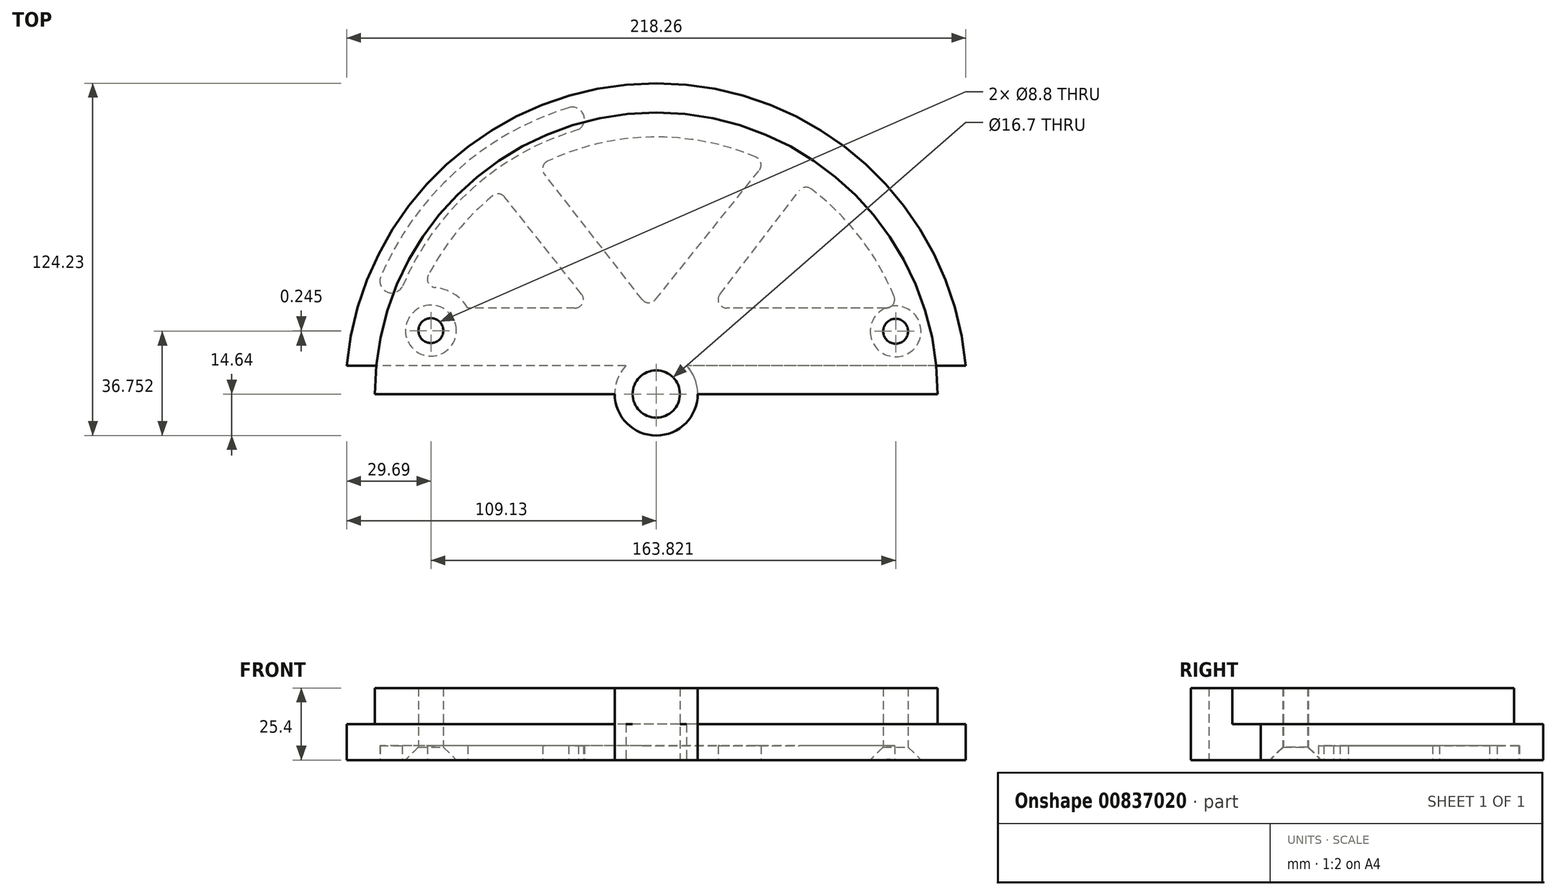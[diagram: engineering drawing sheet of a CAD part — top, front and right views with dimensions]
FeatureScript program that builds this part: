
annotation { "Feature Type Name" : "Feature", "Feature Type Description" : "" }
export const myFeature = defineFeature(function(context is Context, id is Id, definition is map)
    precondition{}
    {
        {
            var Q0;
            Q0=qCreatedBy(makeId("Top.planeOp"),FACE);
            var sketch = newSketch(context, id + "F0", { "sketchPlane" : qUnion([Q0])});
            skArc(sketch, "E0", {"start": v(109.6, 0) * mm, "mid": v(0, 109.6) * mm, "end": v(-109.6, 0) * mm});
            skLineSegment(sketch, "E1", {"start": v(-109.6, 0) * mm, "end": v(109.6, 0) * mm});
            skSolve(sketch);
        }
        {
            var Q0;
            Q0=makeQuery(id+"F0.imprint","IMPRINT",FACE,{"disambiguationData":[TD([[makeQuery(id+"F0.imprint","IMPRINT",EDGE,{"derivedFrom":sQuery(id+"F0.wireOp",EDGE,"E0")}),1.0]])]});
            extrude(context, id + "F1", {"entities" : qUnion([Q0]), "depth" : 12.7 * mm, "offsetDistance" : 25.4 * mm});
        }
        {
            var Q0;
            Q0=qCreatedBy(makeId("Top.planeOp"),FACE);
            var sketch = newSketch(context, id + "F2", { "sketchPlane" : qUnion([Q0])});
            skArc(sketch, "E2", {"start": v(99.24, 0) * mm, "mid": v(0, 99.24) * mm, "end": v(-99.24, 0) * mm});
            skLineSegment(sketch, "E3", {"start": v(99.24, 0) * mm, "end": v(-99.24, 0) * mm});
            skSolve(sketch);
        }
        {
            var Q0;
            Q0=makeQuery(id+"F2.imprint","IMPRINT",FACE,{"disambiguationData":[TD([[makeQuery(id+"F2.imprint","IMPRINT",EDGE,{"derivedFrom":sQuery(id+"F2.wireOp",EDGE,"E2")}),1.0]])]});
            extrude(context, id + "F3", {"entities" : qUnion([Q0]), "operationType" : NewBodyOperationType.ADD, "depth" : 25.4 * mm, "offsetDistance" : 25.4 * mm});
        }
        {
            var Q0;
            Q0=qCreatedBy(makeId("Top.planeOp"),FACE);
            var sketch = newSketch(context, id + "F4", { "sketchPlane" : qUnion([Q0])});
            skLineSegment(sketch, "E4.bottom", {"start": v(116.9, 10.04) * mm, "end": v(-125.87, 10.04) * mm});
            skLineSegment(sketch, "E4.top", {"start": v(116.9, -20) * mm, "end": v(-125.87, -20) * mm});
            skLineSegment(sketch, "E4.left", {"start": v(116.9, 10.04) * mm, "end": v(116.9, -20) * mm});
            skLineSegment(sketch, "E4.right", {"start": v(-125.87, 10.04) * mm, "end": v(-125.87, -20) * mm});
            skSolve(sketch);
        }
        {
            var Q0;
            Q0=makeQuery(id+"F4.imprint","IMPRINT",FACE,{"disambiguationData":[TD([[makeQuery(id+"F4.imprint","IMPRINT",EDGE,{"derivedFrom":sQuery(id+"F4.wireOp",EDGE,"E4.bottom")}),1.0]])]});
            extrude(context, id + "F5", {"entities" : qUnion([Q0]), "operationType" : NewBodyOperationType.REMOVE, "depth" : 12.7 * mm, "offsetDistance" : 25.4 * mm});
        }
        {
            var Q0;
            Q0=qCreatedBy(makeId("Top.planeOp"),FACE);
            var sketch = newSketch(context, id + "F6", { "sketchPlane" : qUnion([Q0])});
            skCircle(sketch, "E5", {"center": v(0, 0) * mm, "radius": 14.64 * mm});
            skSolve(sketch);
        }
        {
            var Q0;
            Q0=makeQuery(id+"F6.imprint","IMPRINT",FACE,{"disambiguationData":[TD([[makeQuery(id+"F6.imprint","IMPRINT",EDGE,{"derivedFrom":sQuery(id+"F6.wireOp",EDGE,"E5")}),1.0]])]});
            extrude(context, id + "F7", {"entities" : qUnion([Q0]), "operationType" : NewBodyOperationType.ADD, "depth" : 25.4 * mm, "offsetDistance" : 25.4 * mm});
        }
        {
            var Q0;
            Q0=qCreatedBy(makeId("Top.planeOp"),FACE);
            var sketch = newSketch(context, id + "F8", { "sketchPlane" : qUnion([Q0])});
            skCircle(sketch, "E6", {"center": v(0, 0) * mm, "radius": 8.35 * mm});
            skSolve(sketch);
        }
        {
            var Q0;
            Q0=makeQuery(id+"F8.imprint","IMPRINT",FACE,{"disambiguationData":[TD([[makeQuery(id+"F8.imprint","IMPRINT",EDGE,{"derivedFrom":sQuery(id+"F8.wireOp",EDGE,"E6")}),1.0]])]});
            extrude(context, id + "F9", {"entities" : qUnion([Q0]), "operationType" : NewBodyOperationType.REMOVE, "depth" : 25.4 * mm, "offsetDistance" : 25.4 * mm});
        }
        {
            var Q0;
            Q0=qCreatedBy(makeId("Top.planeOp"),FACE);
            var sketch = newSketch(context, id + "F10", { "sketchPlane" : qUnion([Q0])});
            skArc(sketch, "E7", {"start": v(83.82, 34.46) * mm, "mid": v(71.76, 55.35) * mm, "end": v(54.62, 72.32) * mm});
            skLineSegment(sketch, "E8", {"start": v(81.04, 30.32) * mm, "end": v(24.8, 30.32) * mm});
            skLineSegment(sketch, "E9", {"start": v(22.42, 35.15) * mm, "end": v(50.43, 71.75) * mm});
            skLineSegment(sketch, "E10", {"start": v(-0.26, 33.28) * mm, "end": v(36.3, 78.9) * mm});
            skLineSegment(sketch, "E11", {"start": v(-4.97, 33.32) * mm, "end": v(-39.44, 77.55) * mm});
            skLineSegment(sketch, "E12", {"start": v(-26.3, 35.18) * mm, "end": v(-53.43, 69.44) * mm});
            skArc(sketch, "E13", {"start": v(-66.42, 30.32) * mm, "mid": v(-71.35, 35.3) * mm, "end": v(-77.97, 37.55) * mm});
            skLineSegment(sketch, "E14.trimOffspring", {"start": v(-28.65, 30.32) * mm, "end": v(-66.42, 30.32) * mm});
            skArc(sketch, "E15.trimOffspring", {"start": v(35.13, 83.54) * mm, "mid": v(-1.76, 90.6) * mm, "end": v(-38.34, 82.11) * mm});
            skArc(sketch, "E16.trimOffspring", {"start": v(-57.69, 69.9) * mm, "mid": v(-70.42, 57.04) * mm, "end": v(-80.35, 41.92) * mm});
            skPoint(sketch, "E17.visualSharp", {"position": v(-2.63, 30.32) * mm});
            skArc(sketch, "E17.filletArc", {"start": v(-4.97, 33.32) * mm, "mid": v(-2.62, 32.16) * mm, "end": v(-0.26, 33.28) * mm});
            skPoint(sketch, "E18.visualSharp", {"position": v(-22.45, 30.32) * mm});
            skArc(sketch, "E18.filletArc", {"start": v(-28.65, 30.32) * mm, "mid": v(-25.95, 32.02) * mm, "end": v(-26.3, 35.18) * mm});
            skPoint(sketch, "E19.visualSharp", {"position": v(18.73, 30.32) * mm});
            skArc(sketch, "E19.filletArc", {"start": v(22.42, 35.15) * mm, "mid": v(22.12, 32) * mm, "end": v(24.8, 30.32) * mm});
            skPoint(sketch, "E20.visualSharp", {"position": v(85.4, 30.32) * mm});
            skArc(sketch, "E20.filletArc", {"start": v(81.04, 30.32) * mm, "mid": v(83.53, 31.65) * mm, "end": v(83.82, 34.46) * mm});
            skPoint(sketch, "E21.visualSharp", {"position": v(52.2, 74.08) * mm});
            skArc(sketch, "E21.filletArc", {"start": v(54.62, 72.32) * mm, "mid": v(52.4, 72.9) * mm, "end": v(50.43, 71.75) * mm});
            skPoint(sketch, "E22.visualSharp", {"position": v(38.74, 81.93) * mm});
            skArc(sketch, "E22.filletArc", {"start": v(36.3, 78.9) * mm, "mid": v(36.88, 81.51) * mm, "end": v(35.13, 83.54) * mm});
            skPoint(sketch, "E23.visualSharp", {"position": v(-41.7, 80.46) * mm});
            skArc(sketch, "E23.filletArc", {"start": v(-38.34, 82.11) * mm, "mid": v(-39.99, 80.1) * mm, "end": v(-39.44, 77.55) * mm});
            skPoint(sketch, "E24.visualSharp", {"position": v(-55.3, 71.8) * mm});
            skArc(sketch, "E24.filletArc", {"start": v(-53.43, 69.44) * mm, "mid": v(-55.46, 70.56) * mm, "end": v(-57.69, 69.9) * mm});
            skPoint(sketch, "E25.visualSharp", {"position": v(-82.6, 37.29) * mm});
            skArc(sketch, "E25.filletArc", {"start": v(-80.35, 41.92) * mm, "mid": v(-80.32, 39.1) * mm, "end": v(-77.97, 37.55) * mm});
            skSolve(sketch);
        }
        {
            var Q0;
            Q0=makeQuery(id+"F10.imprint","IMPRINT",FACE,{"disambiguationData":[TD([[makeQuery(id+"F10.imprint","IMPRINT",EDGE,{"derivedFrom":sQuery(id+"F10.wireOp",EDGE,"E7")}),1.0]])]});
            var Q1;
            Q1=makeQuery(id+"F10.imprint","IMPRINT",FACE,{"disambiguationData":[TD([[makeQuery(id+"F10.imprint","IMPRINT",EDGE,{"derivedFrom":sQuery(id+"F10.wireOp",EDGE,"E10")}),1.0]])]});
            var Q2;
            Q2=makeQuery(id+"F10.imprint","IMPRINT",FACE,{"disambiguationData":[TD([[makeQuery(id+"F10.imprint","IMPRINT",EDGE,{"derivedFrom":sQuery(id+"F10.wireOp",EDGE,"E12")}),1.0]])]});
            extrude(context, id + "F11", {"entities" : qUnion([Q0, Q1, Q2]), "operationType" : NewBodyOperationType.REMOVE, "depth" : 5.08 * mm, "offsetDistance" : 25.4 * mm});
        }
        {
            var Q0;
            Q0=qCreatedBy(makeId("Top.planeOp"),FACE);
            var sketch = newSketch(context, id + "F12", { "sketchPlane" : qUnion([Q0])});
            skArc(sketch, "E26", {"start": v(-27.4, 93.25) * mm, "mid": v(-64.68, 72.55) * mm, "end": v(-89.5, 37.89) * mm});
            skArc(sketch, "E27", {"start": v(-30.91, 100.93) * mm, "mid": v(-70.82, 78.27) * mm, "end": v(-97.34, 40.82) * mm});
            skArc(sketch, "E28", {"start": v(-27.4, 93.25) * mm, "mid": v(-25.72, 98.66) * mm, "end": v(-30.91, 100.93) * mm});
            skArc(sketch, "E29", {"start": v(-97.34, 40.82) * mm, "mid": v(-94.7, 35.94) * mm, "end": v(-89.5, 37.89) * mm});
            skSolve(sketch);
        }
        {
            var Q0;
            Q0=makeQuery(id+"F12.imprint","IMPRINT",FACE,{"disambiguationData":[TD([[makeQuery(id+"F12.imprint","IMPRINT",EDGE,{"derivedFrom":sQuery(id+"F12.wireOp",EDGE,"E26")}),-1.0]])]});
            extrude(context, id + "F13", {"entities" : qUnion([Q0]), "operationType" : NewBodyOperationType.REMOVE, "depth" : 5.08 * mm, "offsetDistance" : 25.4 * mm});
        }
        {
            var Q0;
            Q0=makeQuery(id+"F7.boolean.opBoolean","MERGE",FACE,{"derivedFrom":[makeQuery(id+"F1.opExtrude","CAP_FACE",FACE,{"disambiguationData":[OSD([sQuery(id+"F0.wireOp",EDGE,"E0"),sQuery(id+"F0.wireOp",EDGE,"E1")])],"isStart":true}),makeQuery(id+"F7.opExtrude","CAP_FACE",FACE,{"disambiguationData":[OSD([sQuery(id+"F6.wireOp",EDGE,"E5")])],"isStart":true})]});
            var sketch = newSketch(context, id + "F14", { "sketchPlane" : qUnion([Q0])});
            skPoint(sketch, "E30", {"position": v(84.38, -22.11) * mm});
            skPoint(sketch, "E31", {"position": v(-79.44, -22.36) * mm});
            skSolve(sketch);
        }
        {
            var Q0;
            Q0=sQuery(id+"F14.wireOp",VERTEX,"E30");
            var Q1;
            Q1=sQuery(id+"F14.wireOp",VERTEX,"E31");
            var Q2;
            Q2=makeQuery(id+"F1.opExtrude","SWEPT_BODY",BODY,{"disambiguationData":[OSD([sQuery(id+"F0.wireOp",EDGE,"E0"),sQuery(id+"F0.wireOp",EDGE,"E1")])]});
            hole(context, id + "F15", {"style" : HoleStyle.C_SINK, "endStyle" : HoleEndStyle.THROUGH, "standardTappedOrClearance" : lookupTablePath({ "fit" : "Normal", "standard" : "ISO", "size" : "M8", "type" : "Clearance" }), "standardBlindInLast" : lookupTablePath({ "fit" : "Standard", "standard" : "ISO", "size" : "M8", "type" : "Clearance" }), "holeDiameter" : 8.8 * mm, "cSinkDiameter" : 17.92 * mm, "cSinkAngle" : 90 * degree, "majorDiameter" : 6.35 * mm, "isTappedThrough" : true, "tappedDepth" : 12.7 * mm, "tapClearance" : 3, "startFromSketch" : true, "locations" : qUnion([Q0, Q1]), "scope" : qUnion([Q2])});
        }
    });
